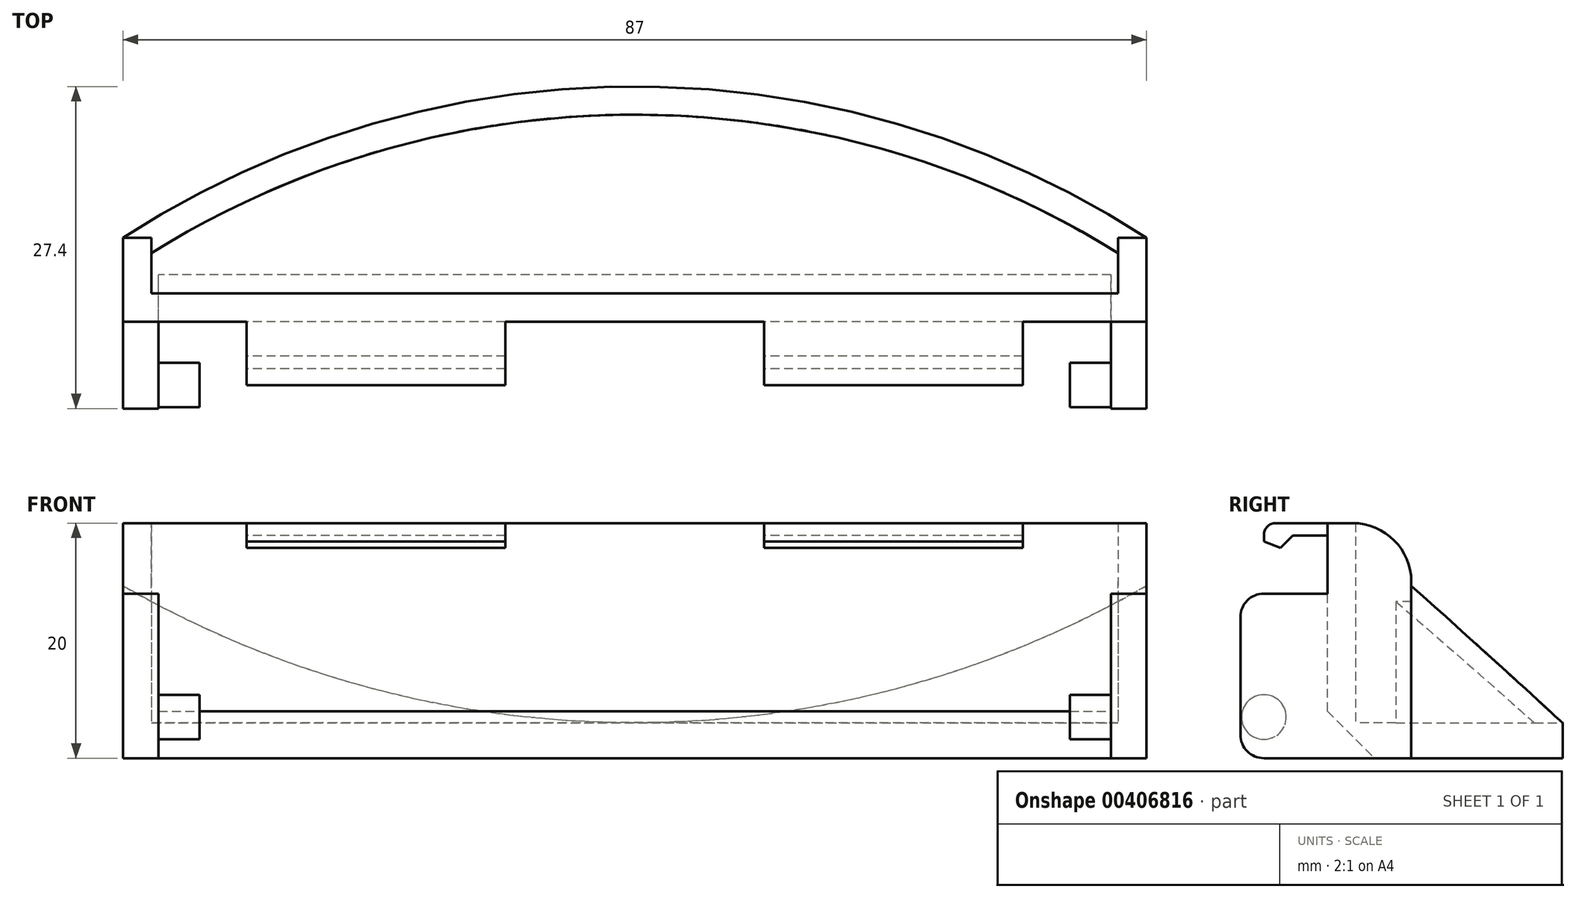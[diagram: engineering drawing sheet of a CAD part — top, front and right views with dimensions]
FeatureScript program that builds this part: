
annotation { "Feature Type Name" : "Feature", "Feature Type Description" : "" }
export const myFeature = defineFeature(function(context is Context, id is Id, definition is map)
    precondition{}
    {
        {
            var Q0;
            Q0=qCreatedBy(makeId("Top.planeOp"),FACE);
            var sketch = newSketch(context, id + "F0", { "sketchPlane" : qUnion([Q0])});
            skLineSegment(sketch, "E0.bottom", {"start": v(0, 0) * mm, "end": v(87, 0) * mm});
            skLineSegment(sketch, "E0.top", {"start": v(0, -20) * mm, "end": v(87, -20) * mm});
            skLineSegment(sketch, "E0.left", {"start": v(0, 0) * mm, "end": v(0, -20) * mm});
            skLineSegment(sketch, "E0.right", {"start": v(87, 0) * mm, "end": v(87, -20) * mm});
            skLineSegment(sketch, "E1", {"start": v(43.5, 0) * mm, "end": v(43.5, -80) * mm});
            skCircle(sketch, "E2", {"center": v(43.5, -80) * mm, "radius": 80 * mm});
            skSolve(sketch);
        }
        {
            var Q0;
            {var subQ0=sQuery(id+"F0.wireOp",EDGE,"E0.left");var subQ1=sQuery(id+"F0.wireOp",EDGE,"E0.top");var subQ2=makeQuery(id+"F0.imprint","INTERSECT",VERTEX,{"derivedFrom":[subQ1,subQ0]});Q0=makeQuery(id+"F0.imprint","IMPRINT",FACE,{"disambiguationData":[TD([[makeQuery(id+"F0.imprint","IMPRINT",EDGE,{"disambiguationData":[TD([[subQ2,-1.0]])],"derivedFrom":subQ1}),1.0]])]});}
            var Q1;
            {var subQ0=sQuery(id+"F0.wireOp",EDGE,"E0.right");var subQ1=sQuery(id+"F0.wireOp",EDGE,"E0.top");var subQ2=makeQuery(id+"F0.imprint","INTERSECT",VERTEX,{"derivedFrom":[subQ1,subQ0]});Q1=makeQuery(id+"F0.imprint","IMPRINT",FACE,{"disambiguationData":[TD([[makeQuery(id+"F0.imprint","IMPRINT",EDGE,{"disambiguationData":[TD([[subQ2,1.0]])],"derivedFrom":subQ1}),1.0]])]});}
            extrude(context, id + "F1", {"entities" : qUnion([Q0, Q1]), "depth" : 3 * mm});
        }
        {
            var Q0;
            Q0=makeQuery(id+"F1.opExtrude","CAP_FACE",FACE,{"disambiguationData":[OSD([sQuery(id+"F0.wireOp",EDGE,"E0.top"),sQuery(id+"F0.wireOp",EDGE,"E0.left"),sQuery(id+"F0.wireOp",EDGE,"E0.right"),sQuery(id+"F0.wireOp",EDGE,"E2")])],"isStart":false});
            var sketch = newSketch(context, id + "F2", { "sketchPlane" : qUnion([Q0])});
            skLineSegment(sketch, "E3.0", {"start": v(2.4, -17.6) * mm, "end": v(84.6, -17.6) * mm});
            skLineSegment(sketch, "E3.1", {"start": v(2.4, -14.18) * mm, "end": v(2.4, -17.6) * mm});
            skArc(sketch, "E3.2", {"start": v(84.6, -14.18) * mm, "mid": v(43.5, -2.4) * mm, "end": v(2.4, -14.18) * mm});
            skLineSegment(sketch, "E3.3", {"start": v(84.6, -17.6) * mm, "end": v(84.6, -14.18) * mm});
            skSolve(sketch);
        }
        {
            var Q0;
            Q0=makeQuery(id+"F2.imprint","IMPRINT",FACE,{"disambiguationData":[TD([[makeQuery(id+"F2.imprint","IMPRINT",EDGE,{"derivedFrom":sQuery(id+"F2.wireOp",EDGE,"E3.0")}),-1.0]])]});
            extrude(context, id + "F3", {"entities" : qUnion([Q0]), "operationType" : NewBodyOperationType.ADD, "depth" : 17 * mm});
        }
        {
            var Q0;
            Q0=qCreatedBy(makeId("Front.planeOp"),FACE);
            var sketch = newSketch(context, id + "F4", { "sketchPlane" : qUnion([Q0])});
            skLineSegment(sketch, "E4.bottom", {"start": v(0, 0) * mm, "end": v(87, 0) * mm});
            skLineSegment(sketch, "E4.top", {"start": v(0, 3) * mm, "end": v(87, 3) * mm});
            skLineSegment(sketch, "E4.left", {"start": v(0, 0) * mm, "end": v(0, 3) * mm});
            skLineSegment(sketch, "E4.right", {"start": v(87, 0) * mm, "end": v(87, 3) * mm});
            skLineSegment(sketch, "E5", {"start": v(43.5, 0) * mm, "end": v(43.5, 90) * mm});
            skCircle(sketch, "E6", {"center": v(43.5, 90) * mm, "radius": 87 * mm});
            skSolve(sketch);
        }
        {
            var Q0;
            Q0=makeQuery(id+"F4.imprint","IMPRINT",FACE,{"disambiguationData":[TD([[makeQuery(id+"F4.imprint","IMPRINT",EDGE,{"derivedFrom":sQuery(id+"F4.wireOp",EDGE,"E6")}),1.0]])]});
            var Q1;
            Q1=makeQuery(id+"F3.opExtrude","SWEPT_FACE",FACE,{"disambiguationData":[OSD([sQuery(id+"F2.wireOp",EDGE,"E3.0")])]});
            extrude(context, id + "F5", {"entities" : qUnion([Q0]), "operationType" : NewBodyOperationType.REMOVE, "endBound" : BoundingType.UP_TO_SURFACE, "endBoundEntityFace" : qUnion([Q1]), "depth" : 25 * mm});
        }
        {
            var Q0;
            {var subQ0=sQuery(id+"F0.wireOp",EDGE,"E0.top");Q0=makeQuery(id+"F3.boolean.opBoolean","MERGE",FACE,{"derivedFrom":[makeQuery(id+"F1.opExtrude","SWEPT_FACE",FACE,{"disambiguationData":[OSD([subQ0])]}),makeQuery(id+"F3.opExtrude","SWEPT_FACE",FACE,{"disambiguationData":[OSD([subQ0])]})]});}
            var sketch = newSketch(context, id + "F6", { "sketchPlane" : qUnion([Q0])});
            skLineSegment(sketch, "E7", {"start": v(43.5, 0) * mm, "end": v(43.5, 35.73) * mm, "construction": true});
            skLineSegment(sketch, "E8.bottom", {"start": v(0, 0) * mm, "end": v(3, 0) * mm});
            skLineSegment(sketch, "E8.top", {"start": v(0, 14) * mm, "end": v(3, 14) * mm});
            skLineSegment(sketch, "E8.left", {"start": v(0, 0) * mm, "end": v(0, 14) * mm});
            skLineSegment(sketch, "E8.right", {"start": v(3, 0) * mm, "end": v(3, 14) * mm});
            skLineSegment(sketch, "E9.MirrorCS", {"start": v(84, 0) * mm, "end": v(84, 14) * mm});
            skLineSegment(sketch, "E10.MirrorCS", {"start": v(87, 14) * mm, "end": v(84, 14) * mm});
            skLineSegment(sketch, "E11.MirrorCS", {"start": v(87, 0) * mm, "end": v(87, 14) * mm});
            skLineSegment(sketch, "E12.MirrorCS", {"start": v(87, 0) * mm, "end": v(84, 0) * mm});
            skLineSegment(sketch, "E13.bottom", {"start": v(10.5, 20) * mm, "end": v(32.5, 20) * mm});
            skLineSegment(sketch, "E13.top", {"start": v(10.5, 17.9) * mm, "end": v(32.5, 17.9) * mm});
            skLineSegment(sketch, "E13.left", {"start": v(10.5, 20) * mm, "end": v(10.5, 17.9) * mm});
            skLineSegment(sketch, "E13.right", {"start": v(32.5, 20) * mm, "end": v(32.5, 17.9) * mm});
            skLineSegment(sketch, "E14.MirrorCS", {"start": v(76.5, 17.9) * mm, "end": v(54.5, 17.9) * mm});
            skLineSegment(sketch, "E15.MirrorCS", {"start": v(76.5, 20) * mm, "end": v(54.5, 20) * mm});
            skLineSegment(sketch, "E16.MirrorCS", {"start": v(54.5, 20) * mm, "end": v(54.5, 17.9) * mm});
            skLineSegment(sketch, "E17.MirrorCS", {"start": v(76.5, 20) * mm, "end": v(76.5, 17.9) * mm});
            skSolve(sketch);
        }
        {
            var Q0;
            Q0=makeQuery(id+"F6.imprint","IMPRINT",FACE,{"disambiguationData":[TD([[makeQuery(id+"F6.imprint","IMPRINT",EDGE,{"derivedFrom":sQuery(id+"F6.wireOp",EDGE,"E8.bottom")}),1.0]])]});
            var Q1;
            Q1=makeQuery(id+"F6.imprint","IMPRINT",FACE,{"disambiguationData":[TD([[makeQuery(id+"F6.imprint","IMPRINT",EDGE,{"derivedFrom":sQuery(id+"F6.wireOp",EDGE,"E9.MirrorCS")}),-1.0]])]});
            extrude(context, id + "F7", {"entities" : qUnion([Q0, Q1]), "operationType" : NewBodyOperationType.ADD, "depth" : 7.4 * mm});
        }
        {
            var Q0;
            Q0=makeQuery(id+"F7.opExtrude","CAP_EDGE",EDGE,{"disambiguationData":[OSD([sQuery(id+"F6.wireOp",EDGE,"E8.bottom")])],"isStart":false});
            var Q1;
            Q1=makeQuery(id+"F7.opExtrude","CAP_EDGE",EDGE,{"disambiguationData":[OSD([sQuery(id+"F6.wireOp",EDGE,"E8.top")])],"isStart":false});
            var Q2;
            Q2=makeQuery(id+"F7.opExtrude","CAP_EDGE",EDGE,{"disambiguationData":[OSD([sQuery(id+"F6.wireOp",EDGE,"E10.MirrorCS")])],"isStart":false});
            var Q3;
            Q3=makeQuery(id+"F7.opExtrude","CAP_EDGE",EDGE,{"disambiguationData":[OSD([sQuery(id+"F6.wireOp",EDGE,"E12.MirrorCS")])],"isStart":false});
            fillet(context, id + "F8", {"entities" : qUnion([Q0, Q1, Q2, Q3]), "radius" : 2 * mm, "tangentPropagation" : true, "allowEdgeOverflow" : false});
        }
        {
            var Q0;
            Q0=makeQuery(id+"F6.imprint","IMPRINT",FACE,{"disambiguationData":[TD([[makeQuery(id+"F6.imprint","IMPRINT",EDGE,{"derivedFrom":sQuery(id+"F6.wireOp",EDGE,"E13.bottom")}),-1.0]])]});
            var Q1;
            Q1=makeQuery(id+"F6.imprint","IMPRINT",FACE,{"disambiguationData":[TD([[makeQuery(id+"F6.imprint","IMPRINT",EDGE,{"derivedFrom":sQuery(id+"F6.wireOp",EDGE,"E14.MirrorCS")}),-1.0]])]});
            extrude(context, id + "F9", {"entities" : qUnion([Q0, Q1]), "operationType" : NewBodyOperationType.ADD, "depth" : 5.4 * mm});
        }
        {
            var Q0;
            Q0=makeQuery(id+"F9.opExtrude","CAP_EDGE",EDGE,{"disambiguationData":[OSD([sQuery(id+"F6.wireOp",EDGE,"E13.bottom")])],"isStart":false});
            var Q1;
            Q1=makeQuery(id+"F9.opExtrude","CAP_EDGE",EDGE,{"disambiguationData":[OSD([sQuery(id+"F6.wireOp",EDGE,"E15.MirrorCS")])],"isStart":false});
            fillet(context, id + "F10", {"entities" : qUnion([Q0, Q1]), "radius" : 1 * mm, "tangentPropagation" : true, "allowEdgeOverflow" : false});
        }
        {
            var Q0;
            Q0=makeQuery(id+"F9.opExtrude","SWEPT_FACE",FACE,{"disambiguationData":[OSD([sQuery(id+"F6.wireOp",EDGE,"E13.left")])]});
            var sketch = newSketch(context, id + "F11", { "sketchPlane" : qUnion([Q0])});
            skPoint(sketch, "E18.centerSnap0", {"position": v(25.4, 18.45) * mm});
            skLineSegment(sketch, "E19.bottom", {"start": v(24.4, 20) * mm, "end": v(20.4, 20) * mm});
            skPoint(sketch, "E20", {"position": v(22.7, 17.9) * mm});
            skLineSegment(sketch, "E21", {"start": v(20, 18.95) * mm, "end": v(22.95, 18.95) * mm});
            skLineSegment(sketch, "E22", {"start": v(22.95, 18.95) * mm, "end": v(24, 17.9) * mm});
            skLineSegment(sketch, "E23", {"start": v(24, 17.9) * mm, "end": v(25.4, 18.45) * mm});
            skSolve(sketch);
        }
        {
            var Q0;
            Q0=makeQuery(id+"F1.opExtrude","CAP_EDGE",EDGE,{"disambiguationData":[OSD([sQuery(id+"F0.wireOp",EDGE,"E0.top")])],"isStart":true});
            chamfer(context, id + "F12", {"entities" : qUnion([Q0]), "width" : 4 * mm, "tangentPropagation" : true});
        }
        {
            var Q0;
            Q0=makeQuery(id+"F7.opExtrude","SWEPT_FACE",FACE,{"disambiguationData":[OSD([sQuery(id+"F6.wireOp",EDGE,"E8.right")])]});
            var sketch = newSketch(context, id + "F13", { "sketchPlane" : qUnion([Q0])});
            skLineSegment(sketch, "E24.bottom", {"start": v(-27.4, 2) * mm, "end": v(-25.4, 2) * mm});
            skLineSegment(sketch, "E24.top", {"start": v(-27.4, 0) * mm, "end": v(-25.4, 0) * mm});
            skLineSegment(sketch, "E24.left", {"start": v(-27.4, 2) * mm, "end": v(-27.4, 0) * mm});
            skLineSegment(sketch, "E24.right", {"start": v(-25.4, 2) * mm, "end": v(-25.4, 0) * mm});
            skLineSegment(sketch, "E25", {"start": v(-25.4, 2) * mm, "end": v(-25.4, 3.5) * mm});
            skCircle(sketch, "E26", {"center": v(-25.4, 3.5) * mm, "radius": 1.9 * mm});
            skSolve(sketch);
        }
        {
            var Q0;
            Q0=makeQuery(id+"F13.imprint","IMPRINT",FACE,{"disambiguationData":[TD([[makeQuery(id+"F13.imprint","IMPRINT",EDGE,{"derivedFrom":sQuery(id+"F13.wireOp",EDGE,"E26")}),1.0]])]});
            extrude(context, id + "F14", {"entities" : qUnion([Q0]), "depth" : 3.5 * mm});
        }
        {
            var Q0;
            {var subQ0=sQuery(id+"F0.wireOp",EDGE,"E0.top");Q0=makeQuery(id+"F12.opChamfer","BLEND_EDGE",EDGE,{"blendedFrom":[makeQuery(id+"F1.opExtrude","CAP_EDGE",EDGE,{"disambiguationData":[OSD([subQ0])],"isStart":true}),makeQuery(id+"F7.boolean.opBoolean","MERGE",FACE,{"derivedFrom":[makeQuery(id+"F1.opExtrude","CAP_FACE",FACE,{"disambiguationData":[OSD([subQ0,sQuery(id+"F0.wireOp",EDGE,"E0.left"),sQuery(id+"F0.wireOp",EDGE,"E0.right"),sQuery(id+"F0.wireOp",EDGE,"E2")])],"isStart":true}),makeQuery(id+"F7.opExtrude","SWEPT_FACE",FACE,{"disambiguationData":[OSD([sQuery(id+"F6.wireOp",EDGE,"E8.bottom")])]}),makeQuery(id+"F7.opExtrude","SWEPT_FACE",FACE,{"disambiguationData":[OSD([sQuery(id+"F6.wireOp",EDGE,"E12.MirrorCS")])]})]})],"blendedInto":[makeQuery(id+"F7.boolean.opBoolean","MERGE",FACE,{"derivedFrom":[makeQuery(id+"F1.opExtrude","CAP_FACE",FACE,{"disambiguationData":[OSD([subQ0,sQuery(id+"F0.wireOp",EDGE,"E0.left"),sQuery(id+"F0.wireOp",EDGE,"E0.right"),sQuery(id+"F0.wireOp",EDGE,"E2")])],"isStart":true}),makeQuery(id+"F7.opExtrude","SWEPT_FACE",FACE,{"disambiguationData":[OSD([sQuery(id+"F6.wireOp",EDGE,"E8.bottom")])]}),makeQuery(id+"F7.opExtrude","SWEPT_FACE",FACE,{"disambiguationData":[OSD([sQuery(id+"F6.wireOp",EDGE,"E12.MirrorCS")])]})]})]});}
            cPoint(context, id + "F15", {"entities" : qUnion([Q0]), "parameter" : 0.5});
        }
        {
            var Q0;
            Q0=qCreatedBy(makeId("Right.planeOp"),FACE);
            var Q1;
            Q1 = qCreatedBy(id + "F15" ,VERTEX);
            cPlane(context, id + "F16", {"entities" : qUnion([Q0, Q1]), "cplaneType" : CPlaneType.PLANE_POINT, "offset" : 25 * mm, "width" : 150 * mm, "height" : 150 * mm});
        }
        {
            var Q0;
            Q0=makeQuery(id+"F14.opExtrude","SWEPT_BODY",BODY,{"disambiguationData":[OSD([sQuery(id+"F13.wireOp",EDGE,"E26")])]});
            var Q1;
            Q1=qCreatedBy(id+"F16.planeOp",FACE);
            mirror(context, id + "F17", {"operationType" : NewBodyOperationType.ADD, "entities" : qUnion([Q0]), "mirrorPlane" : qUnion([Q1])});
        }
        {
            var Q0;
            {var subQ0=sQuery(id+"F11.wireOp",EDGE,"E21");Q0=makeQuery(id+"F11.imprint","IMPRINT",FACE,{"disambiguationData":[TD([[makeQuery(id+"F11.imprint","IMPRINT",EDGE,{"derivedFrom":subQ0}),-1.0]])]});}
            var Q1;
            {var subQ0=sQuery(id+"F11.wireOp",EDGE,"E23");Q1=makeQuery(id+"F11.imprint","IMPRINT",FACE,{"disambiguationData":[TD([[makeQuery(id+"F11.imprint","IMPRINT",EDGE,{"derivedFrom":subQ0}),-1.0]])]});}
            var Q2;
            Q2=makeQuery(id+"F9.opExtrude","SWEPT_FACE",FACE,{"disambiguationData":[OSD([sQuery(id+"F6.wireOp",EDGE,"E17.MirrorCS")])]});
            extrude(context, id + "F18", {"entities" : qUnion([Q0, Q1]), "operationType" : NewBodyOperationType.REMOVE, "endBound" : BoundingType.UP_TO_SURFACE, "oppositeDirection" : true, "endBoundEntityFace" : qUnion([Q2]), "depth" : 25 * mm});
        }
        {
            var Q0;
            Q0=makeQuery(id+"F5.boolean.opBoolean","MERGE",FACE,{"derivedFrom":[makeQuery(id+"F3.opExtrude","SWEPT_FACE",FACE,{"disambiguationData":[OSD([sQuery(id+"F2.wireOp",EDGE,"E3.0")])]})],"fromTools":[makeQuery(id+"F5.opExtrude","CAP_FACE",FACE,{"disambiguationData":[OSD([sQuery(id+"F4.wireOp",EDGE,"E6")])],"isStart":false})]});
            var sketch = newSketch(context, id + "F19", { "sketchPlane" : qUnion([Q0])});
            skLineSegment(sketch, "E27", {"start": v(-2.4, 13.32) * mm, "end": v(-2.4, 20) * mm});
            skLineSegment(sketch, "E28", {"start": v(-84.6, 13.32) * mm, "end": v(-84.6, 20) * mm});
            skSolve(sketch);
        }
        {
            var Q0;
            {var subQ0=sQuery(id+"F19.wireOp",EDGE,"E28");Q0=makeQuery(id+"F19.imprint","IMPRINT",FACE,{"disambiguationData":[TD([[makeQuery(id+"F19.imprint","IMPRINT",EDGE,{"derivedFrom":subQ0}),1.0]])]});}
            var Q1;
            {var subQ0=sQuery(id+"F19.wireOp",EDGE,"E27");Q1=makeQuery(id+"F19.imprint","IMPRINT",FACE,{"disambiguationData":[TD([[makeQuery(id+"F19.imprint","IMPRINT",EDGE,{"derivedFrom":subQ0}),-1.0]])]});}
            var Q2;
            {var subQ0=sQuery(id+"F0.wireOp",EDGE,"E2");var subQ1=sQuery(id+"F0.wireOp",EDGE,"E0.right");Q2=makeQuery(id+"F5.boolean.opBoolean","INTERSECT",VERTEX,{"derivedFrom":[makeQuery(id+"F3.boolean.opBoolean","MERGE",FACE,{"derivedFrom":[makeQuery(id+"F1.opExtrude","SWEPT_FACE",FACE,{"disambiguationData":[OSD([subQ1])]}),makeQuery(id+"F3.opExtrude","SWEPT_FACE",FACE,{"disambiguationData":[OSD([subQ1])]})]}),makeQuery(id+"F3.boolean.opBoolean","MERGE",FACE,{"derivedFrom":[makeQuery(id+"F1.opExtrude","SWEPT_FACE",FACE,{"disambiguationData":[OSD([subQ0])]}),makeQuery(id+"F3.opExtrude","SWEPT_FACE",FACE,{"disambiguationData":[OSD([subQ0])]})]}),makeQuery(id+"F5.opExtrude","SWEPT_FACE",FACE,{"disambiguationData":[OSD([sQuery(id+"F4.wireOp",EDGE,"E6")])]})]});}
            extrude(context, id + "F20", {"entities" : qUnion([Q0, Q1]), "operationType" : NewBodyOperationType.ADD, "endBound" : BoundingType.UP_TO_VERTEX, "endBoundEntityVertex" : qUnion([Q2]), "depth" : 25 * mm});
        }
        {
            var Q0;
            {var subQ0=sQuery(id+"F4.wireOp",EDGE,"E6");var subQ1=makeQuery(id+"F5.opExtrude","CAP_FACE",FACE,{"disambiguationData":[OSD([subQ0])],"isStart":false});var subQ2=sQuery(id+"F0.wireOp",EDGE,"E0.right");var subQ3=sQuery(id+"F2.wireOp",EDGE,"E3.3");var subQ4=sQuery(id+"F2.wireOp",EDGE,"E3.2");var subQ5=sQuery(id+"F2.wireOp",EDGE,"E3.1");var subQ6=sQuery(id+"F2.wireOp",EDGE,"E3.0");var subQ7=sQuery(id+"F0.wireOp",EDGE,"E2");var subQ8=sQuery(id+"F0.wireOp",EDGE,"E0.left");var subQ9=sQuery(id+"F0.wireOp",EDGE,"E0.top");var subQ10=makeQuery(id+"F5.boolean.opBoolean","INTERSECT",EDGE,{"derivedFrom":[makeQuery(id+"F3.opExtrude","CAP_FACE",FACE,{"disambiguationData":[OSD([subQ9,subQ8,subQ2,subQ7,subQ6,subQ5,subQ4,subQ3])],"isStart":false}),subQ1]});Q0=makeQuery(id+"F20.opExtrude","CAP_EDGE",EDGE,{"disambiguationData":[OSD([subQ9,subQ8,subQ2,subQ7,subQ6,subQ5,subQ4,subQ3,subQ0]),TDD([makeQuery(id+"F19.imprint","IMPRINT",EDGE,{"disambiguationData":[TD([[makeQuery(id+"F19.imprint","INTERSECT",VERTEX,{"derivedFrom":[subQ10,sQuery(id+"F19.wireOp",EDGE,"E28")]}),-1.0]])],"derivedFrom":subQ10})])],"isStart":false});}
            fillet(context, id + "F21", {"entities" : qUnion([Q0]), "radius" : 5 * mm, "tangentPropagation" : true, "allowEdgeOverflow" : false});
        }
    });
